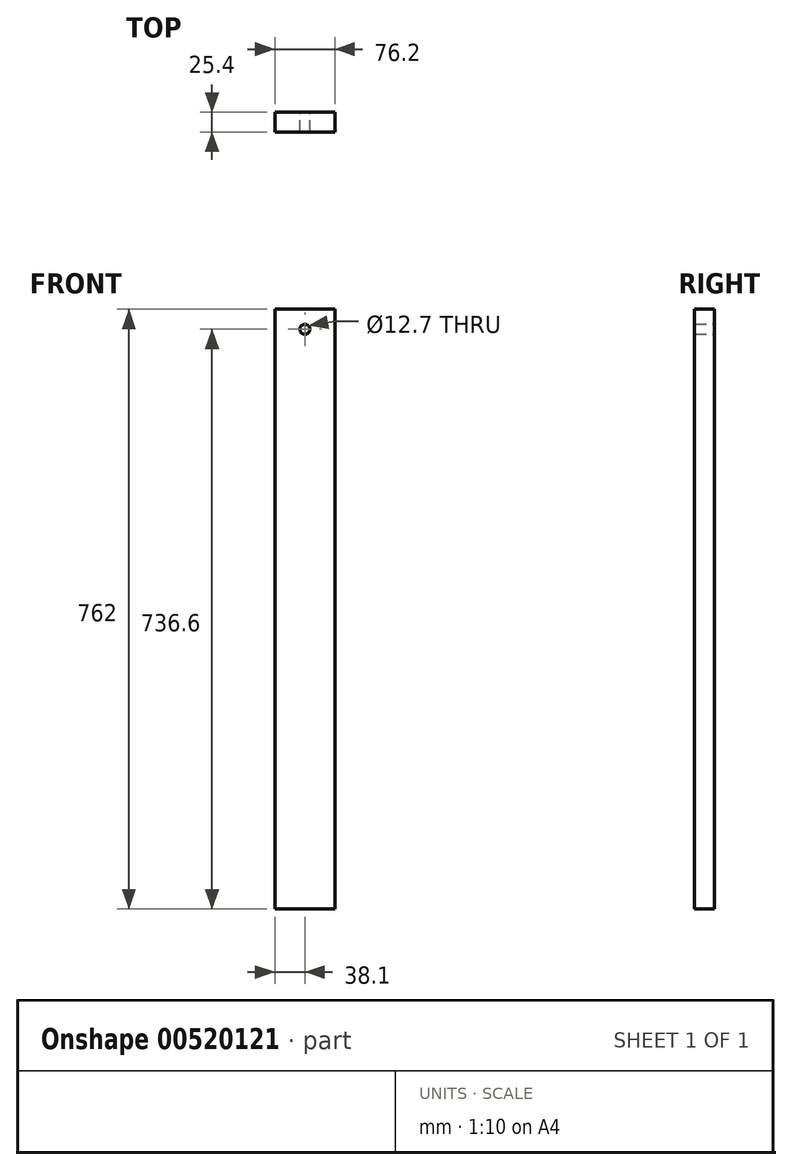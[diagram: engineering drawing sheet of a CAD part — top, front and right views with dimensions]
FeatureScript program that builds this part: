
annotation { "Feature Type Name" : "Feature", "Feature Type Description" : "" }
export const myFeature = defineFeature(function(context is Context, id is Id, definition is map)
    precondition{}
    {
        {
            var Q0;
            Q0=qCreatedBy(makeId("Front.planeOp"),FACE);
            var sketch = newSketch(context, id + "F0", { "sketchPlane" : qUnion([Q0])});
            skLineSegment(sketch, "E0", {"start": v(0, 0) * mm, "end": v(0, -762) * mm});
            skLineSegment(sketch, "E1", {"start": v(0, -762) * mm, "end": v(76.2, -762) * mm});
            skLineSegment(sketch, "E2", {"start": v(76.2, -762) * mm, "end": v(76.2, 0) * mm});
            skLineSegment(sketch, "E3", {"start": v(76.2, 0) * mm, "end": v(0, 0) * mm});
            skCircle(sketch, "E4", {"center": v(38.1, -25.4) * mm, "radius": 6.35 * mm});
            skSolve(sketch);
        }
        {
            var Q0;
            Q0=makeQuery(id+"F0.imprint","IMPRINT",FACE,{"disambiguationData":[TD([[makeQuery(id+"F0.imprint","IMPRINT",EDGE,{"derivedFrom":sQuery(id+"F0.wireOp",EDGE,"E0")}),1.0]])]});
            extrude(context, id + "F1", {"entities" : qUnion([Q0]), "depth" : 25.4 * mm, "offsetDistance" : 25.4 * mm});
        }
    });
